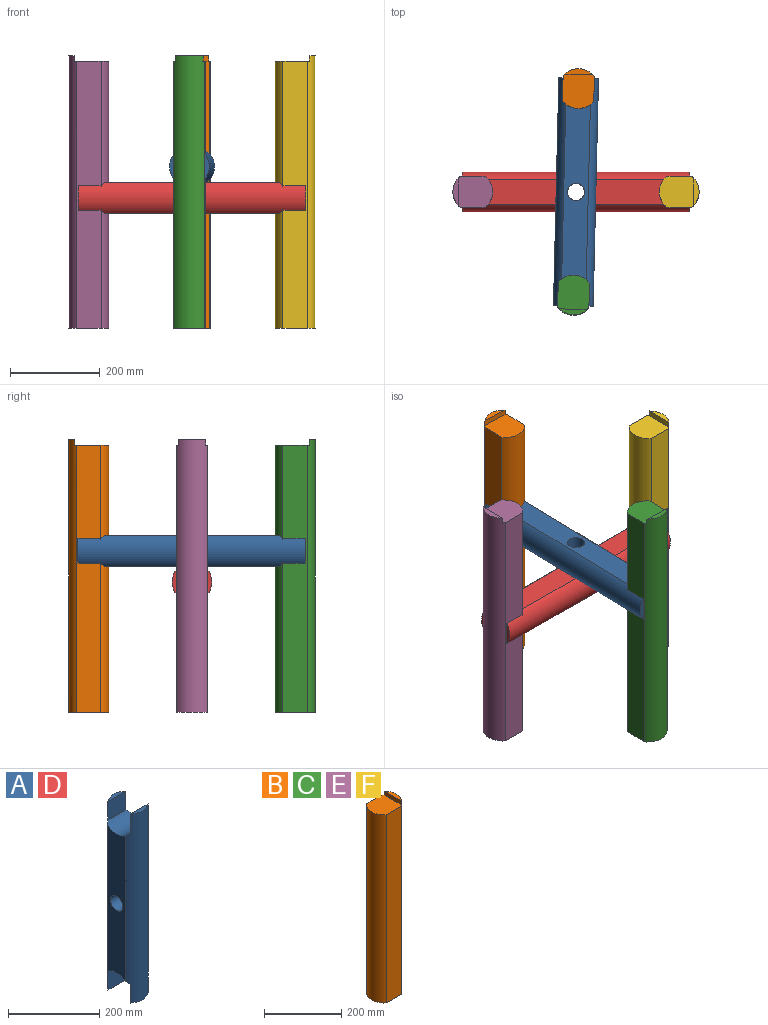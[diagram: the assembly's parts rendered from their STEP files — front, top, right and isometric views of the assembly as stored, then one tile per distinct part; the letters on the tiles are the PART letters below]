
ASSEMBLY  parts=6 mates=14
PART A: 15 faces, bbox 69.9x88.9x508 mm
  f0: plane 391.54x54.99mm, normal (-1,0,0), area 19677mm2, adj f2,f4,f12,f13,f14
  f1: plane 391.54x54.99mm, normal (1,0,0), area 19677mm2, adj f2,f4,f12,f13,f14
  f2: cylinder r=44.45mm len=508mm, axis (0,0,-1), area 38516.5mm2, adj f0,f1,f6,f7,f8,f10,f12,f13
  f3: plane 54.99x9.53mm, normal (0,0,-1), area 357.4mm2, adj f4,f11
  f4: cylinder r=44.45mm len=508mm, axis (0,0,-1), area 38516.5mm2, adj f0,f1,f3,f5,f9,f11,f12,f13
  f5: plane 54.99x9.53mm, normal (0,0,1), area 357.4mm2, adj f4,f9
  f6: plane 54.99x9.53mm, normal (0,0,1), area 357.4mm2, adj f2,f8
  f7: plane 54.99x9.53mm, normal (0,0,-1), area 357.4mm2, adj f2,f10
  f8: plane 54.99x50.8mm, normal (0,1,0), area 2793.6mm2, adj f2,f6,f13
  f9: plane 54.99x50.8mm, normal (0,-1,0), area 2793.6mm2, adj f4,f5,f13
  f10: plane 54.99x50.8mm, normal (0,1,0), area 2793.6mm2, adj f2,f7,f12
  f11: plane 54.99x50.8mm, normal (0,-1,0), area 2793.6mm2, adj f3,f4,f12
  f12: cylinder r=44.45mm len=69.85mm, axis (-1,0,0), area 5462.3mm2, adj f0,f1,f2,f4,f10,f11
  f13: cylinder r=44.45mm len=69.85mm, axis (-1,0,0), area 5462.3mm2, adj f0,f1,f2,f4,f8,f9
  f14: cylinder r=19.05mm len=69.85mm, axis (-1,0,0), area 8360.7mm2, adj f0,f1
PART B: 8 faces, bbox 88.9x69.9x609.6 mm
  f0: plane 596.9x54.99mm, normal (0,-1,0), area 32825.1mm2, adj f1,f2,f5,f6
  f1: cylinder r=44.45mm len=609.6mm, axis (0,0,-1), area 48837.5mm2, adj f0,f3,f4,f5,f6,f7
  f2: cylinder r=44.45mm len=596.9mm, axis (0,0,-1), area 47962.3mm2, adj f0,f4,f5,f6
  f3: plane 62.22x12.7mm, normal (0,0,1), area 543.9mm2, adj f1,f7
  f4: plane 596.9x54.99mm, normal (0,1,0), area 32825.1mm2, adj f1,f2,f5,f6
  f5: plane 88.9x69.85mm, normal (0,0,-1), area 5492.3mm2, adj f0,f1,f2,f4
  f6: plane 76.2x69.85mm, normal (0,0,1), area 4948.3mm2, adj f0,f1,f2,f4,f7
  f7: plane 62.22x12.7mm, normal (-1,0,0), area 790.2mm2, adj f1,f3,f6
PART C: same geometry as B
PART D: same geometry as A
PART E: same geometry as B
PART F: same geometry as B
PLACE A rot(axis=(-0.57,0.59,0.57),119.2deg) t=(-236.7,-253.93,361.34)mm
PLACE B rot(axis=(0,0,1),88.6deg) t=(-225.25,230.63,0)mm
PLACE C rot(axis=(0,0,-1),91.4deg) t=(-236.15,-230.63,0)mm
PLACE D rot(axis=(0,1,0),90deg) t=(-484.7,0,291.49)mm
PLACE E rot(axis=(0,0,-1),180deg) t=(-461.39,0,0)mm
PLACE F at identity fixed
MATE cylindrical D.f13 <-> F.f2  axis (0,0,1) through (0,0,291.49)mm
MATE planar B.f6 <-> F.f6  axis (0,0,1) through (-225.34,226.58,596.9)mm
MATE planar D.f9 <-> F.f4  axis (0,-1,0) through (-2.1,34.93,291.49)mm
MATE planar E.f6 <-> F.f6  axis (0,0,1) through (-457.34,0,596.9)mm
MATE cylindrical A.f12 <-> C.f2  axis (0,0,1) through (-236.15,-230.63,361.34)mm
MATE cylindrical A.f14 <-> D.f14  axis (0,0,1) through (-230.7,0,361.34)mm
MATE planar A.f8 <-> B.f0  axis (-1,0.02,0) through (-190.38,227.71,361.34)mm
MATE planar E.f0 <-> D.f11  axis (0,1,0) through (-461.39,34.93,298.45)mm
MATE planar A.f11 <-> C.f0  axis (1,-0.02,0) through (-271.01,-227.71,361.34)mm
MATE cylindrical D.f12 <-> E.f2  axis (0,0,1) through (-461.39,0,291.49)mm
MATE planar A.f14 <-> D.f14  axis (0,0,-1) through (-230.7,0,326.42)mm
MATE cylindrical B.f2 <-> A.f13  axis (0,0,-1) through (-225.25,230.63,298.45)mm
MATE planar E.f6 <-> F.f6  axis (0,0,1) through (-457.34,0,596.9)mm
MATE planar C.f2 <-> F.f6  axis (0,0,1) through (-236.15,-230.63,596.9)mm
